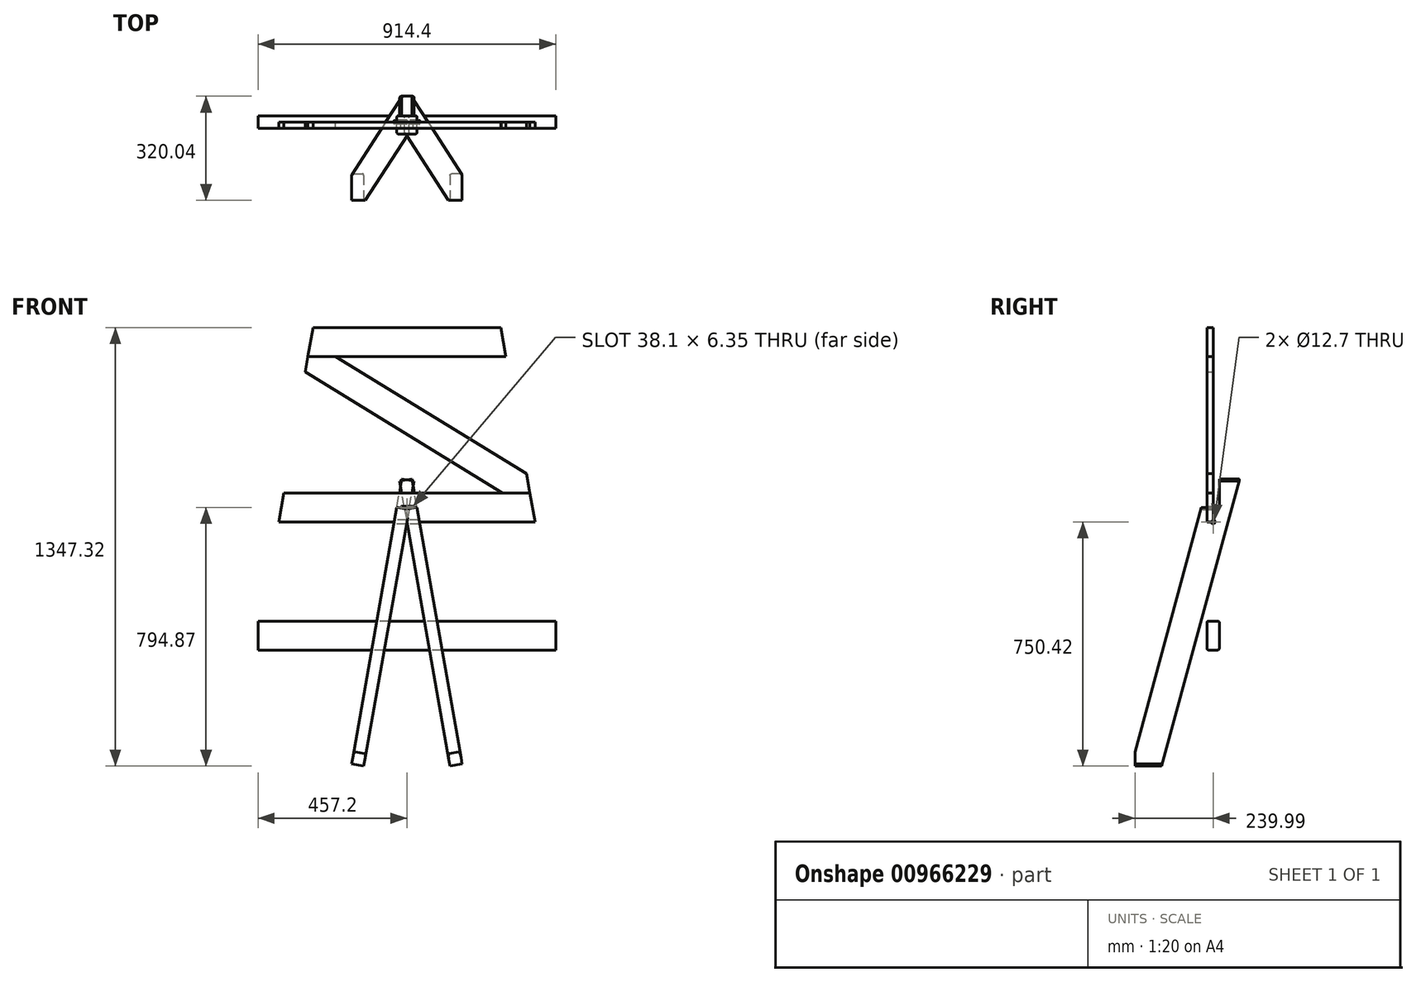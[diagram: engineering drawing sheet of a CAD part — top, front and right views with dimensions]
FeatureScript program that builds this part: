
annotation { "Feature Type Name" : "Feature", "Feature Type Description" : "" }
export const myFeature = defineFeature(function(context is Context, id is Id, definition is map)
    precondition{}
    {
        {
            var Q0;
            Q0=qCreatedBy(makeId("Front.planeOp"),FACE);
            var sketch = newSketch(context, id + "F0", { "sketchPlane" : qUnion([Q0])});
            skLineSegment(sketch, "E0", {"start": v(0, 0) * mm, "end": v(74.84, 13.2) * mm, "construction": true});
            skLineSegment(sketch, "E1", {"start": v(0, 0) * mm, "end": v(74.84, 0) * mm, "construction": true});
            skLineSegment(sketch, "E2", {"start": v(0, 0) * mm, "end": v(74.84, -13.2) * mm, "construction": true});
            skSolve(sketch);
        }
        {
            var Q0;
            Q0=sQuery(id+"F0.wireOp",EDGE,"E0");
            var Q1;
            Q1=sQuery(id+"F0.wireOp",VERTEX,"E0.start");
            cPlane(context, id + "F1", {"entities" : qUnion([Q0, Q1]), "cplaneType" : CPlaneType.LINE_POINT, "offset" : 25.4 * mm, "width" : 152.4 * mm, "height" : 152.4 * mm});
        }
        {
            var Q0;
            Q0=sQuery(id+"F0.wireOp",EDGE,"E2");
            var Q1;
            Q1=sQuery(id+"F0.wireOp",VERTEX,"E0.start");
            cPlane(context, id + "F2", {"entities" : qUnion([Q0, Q1]), "cplaneType" : CPlaneType.LINE_POINT, "offset" : 25.4 * mm, "width" : 152.4 * mm, "height" : 152.4 * mm});
        }
        {
            var Q0;
            Q0=qCreatedBy(id+"F1.planeOp",FACE);
            var sketch = newSketch(context, id + "F3", { "sketchPlane" : qUnion([Q0])});
            skLineSegment(sketch, "E3", {"start": v(10.2, 38.1) * mm, "end": v(-204.18, -762) * mm, "construction": true});
            skLineSegment(sketch, "E4", {"start": v(0, 0) * mm, "end": v(0, -762) * mm, "construction": true});
            skLineSegment(sketch, "E5.0", {"start": v(-35.8, 38.1) * mm, "end": v(-239.99, -723.9) * mm});
            skLineSegment(sketch, "E6.0", {"start": v(80.05, 127) * mm, "end": v(-158.16, -762) * mm});
            skLineSegment(sketch, "E7", {"start": v(-158.16, -762) * mm, "end": v(0, -762) * mm, "construction": true});
            skLineSegment(sketch, "E8", {"start": v(0, 0) * mm, "end": v(0, 239.53) * mm, "construction": true});
            skLineSegment(sketch, "E9.0", {"start": v(19.05, 38.1) * mm, "end": v(19.05, 127) * mm});
            skLineSegment(sketch, "E10", {"start": v(-35.8, 38.1) * mm, "end": v(19.05, 38.1) * mm});
            skLineSegment(sketch, "E11", {"start": v(19.05, 127) * mm, "end": v(80.05, 127) * mm});
            skLineSegment(sketch, "E12", {"start": v(-239.99, -723.9) * mm, "end": v(-239.99, -762) * mm});
            skPoint(sketch, "E13.orphan", {"position": v(-250.2, -762) * mm});
            skLineSegment(sketch, "E14", {"start": v(-158.16, -762) * mm, "end": v(-239.99, -762) * mm});
            skLineSegment(sketch, "E15", {"start": v(-149.99, 0) * mm, "end": v(149.99, 0) * mm, "construction": true});
            skSolve(sketch);
        }
        {
            var Q0;
            Q0=qCreatedBy(id+"F2.planeOp",FACE);
            var sketch = newSketch(context, id + "F4", { "sketchPlane" : qUnion([Q0])});
            skLineSegment(sketch, "E16", {"start": v(10.2, 38.1) * mm, "end": v(-204.18, -762) * mm, "construction": true});
            skLineSegment(sketch, "E17", {"start": v(0, 0) * mm, "end": v(0, -762) * mm, "construction": true});
            skLineSegment(sketch, "E18.0", {"start": v(-35.8, 38.1) * mm, "end": v(-239.99, -723.9) * mm});
            skLineSegment(sketch, "E19.0", {"start": v(80.05, 127) * mm, "end": v(-158.16, -762) * mm});
            skLineSegment(sketch, "E20", {"start": v(-158.16, -762) * mm, "end": v(0, -762) * mm, "construction": true});
            skLineSegment(sketch, "E21", {"start": v(0, 0) * mm, "end": v(0, 499.08) * mm, "construction": true});
            skLineSegment(sketch, "E22.0", {"start": v(19.05, 38.1) * mm, "end": v(19.05, 127) * mm});
            skLineSegment(sketch, "E23", {"start": v(-35.8, 38.1) * mm, "end": v(19.05, 38.1) * mm});
            skLineSegment(sketch, "E24", {"start": v(19.05, 127) * mm, "end": v(80.05, 127) * mm});
            skLineSegment(sketch, "E25", {"start": v(-239.99, -723.9) * mm, "end": v(-239.99, -762) * mm});
            skPoint(sketch, "E26.orphan", {"position": v(-250.2, -762) * mm});
            skLineSegment(sketch, "E27", {"start": v(-158.16, -762) * mm, "end": v(-239.99, -762) * mm});
            skLineSegment(sketch, "E28", {"start": v(-106.86, 0) * mm, "end": v(106.86, 0) * mm, "construction": true});
            skSolve(sketch);
        }
        {
            var Q0;
            Q0 = qSketchRegion(id + "F3", true);
            extrude(context, id + "F5", {"entities" : qUnion([Q0]), "depth" : 38.1 * mm, "offsetDistance" : 25.4 * mm});
        }
        {
            var Q0;
            Q0 = qSketchRegion(id + "F4", true);
            extrude(context, id + "F6", {"entities" : qUnion([Q0]), "oppositeDirection" : true, "depth" : 38.1 * mm, "offsetDistance" : 25.4 * mm});
        }
        {
            var Q0;
            Q0=makeQuery(id+"F5.opExtrude","SWEPT_EDGE",EDGE,{"disambiguationData":[OSD([sQuery(id+"F3.wireOp",EDGE,"E9.0"),sQuery(id+"F3.wireOp",EDGE,"E10")])]});
            var Q1;
            Q1=makeQuery(id+"F6.opExtrude","SWEPT_EDGE",EDGE,{"disambiguationData":[OSD([sQuery(id+"F4.wireOp",EDGE,"E22.0"),sQuery(id+"F4.wireOp",EDGE,"E23")])]});
            fillet(context, id + "F7", {"entities" : qUnion([Q0, Q1]), "tangentPropagation" : true, "radius" : 6.35 * mm, "defaultsChanged" : false, "vertexSettings" : [], "allowEdgeOverflow" : false});
        }
        {
            var Q0;
            Q0=qCreatedBy(makeId("Right.planeOp"),FACE);
            var sketch = newSketch(context, id + "F8", { "sketchPlane" : qUnion([Q0])});
            skCircle(sketch, "E29", {"center": v(0, 0) * mm, "radius": 6.35 * mm});
            skSolve(sketch);
        }
        {
            var Q0;
            Q0 = qSketchRegion(id + "F8", true);
            extrude(context, id + "F9", {"entities" : qUnion([Q0]), "operationType" : NewBodyOperationType.REMOVE, "endBound" : BoundingType.THROUGH_ALL, "depth" : 25.4 * mm, "offsetDistance" : 25.4 * mm, "hasSecondDirection" : true, "secondDirectionBound" : SecondDirectionBoundingType.THROUGH_ALL, "secondDirectionOppositeDirection" : true, "secondDirectionDepth" : 25.4 * mm});
        }
        {
            var Q0;
            Q0=qCreatedBy(makeId("Front.planeOp"),FACE);
            var sketch = newSketch(context, id + "F10", { "sketchPlane" : qUnion([Q0])});
            skLineSegment(sketch, "E30.0", {"start": v(-378.02, 88.9) * mm, "end": v(378.02, 88.9) * mm});
            skLineSegment(sketch, "E31.0", {"start": v(-393.7, 0) * mm, "end": v(393.7, 0) * mm});
            skLineSegment(sketch, "E32", {"start": v(-393.7, 0) * mm, "end": v(-378.02, 88.9) * mm});
            skLineSegment(sketch, "E33", {"start": v(378.02, 88.9) * mm, "end": v(393.7, 0) * mm});
            skLineSegment(sketch, "E34.bottom", {"start": v(15.87, 41.27) * mm, "end": v(-15.88, 41.27) * mm});
            skLineSegment(sketch, "E34.top", {"start": v(15.87, 47.62) * mm, "end": v(-15.88, 47.62) * mm});
            skLineSegment(sketch, "E34.left", {"start": v(19.05, 44.45) * mm, "end": v(19.05, 44.45) * mm});
            skLineSegment(sketch, "E34.right", {"start": v(-19.05, 44.45) * mm, "end": v(-19.05, 44.45) * mm});
            skPoint(sketch, "E34.middle", {"position": v(0, 44.45) * mm});
            skPoint(sketch, "E35.visualSharp", {"position": v(-19.05, 47.62) * mm});
            skArc(sketch, "E35.filletArc", {"start": v(-15.88, 47.62) * mm, "mid": v(-18.12, 46.7) * mm, "end": v(-19.05, 44.45) * mm});
            skPoint(sketch, "E36.visualSharp", {"position": v(-19.05, 41.27) * mm});
            skArc(sketch, "E36.filletArc", {"start": v(-19.05, 44.45) * mm, "mid": v(-18.12, 42.2) * mm, "end": v(-15.88, 41.27) * mm});
            skPoint(sketch, "E37.visualSharp", {"position": v(19.05, 41.27) * mm});
            skArc(sketch, "E37.filletArc", {"start": v(15.87, 41.27) * mm, "mid": v(18.12, 42.2) * mm, "end": v(19.05, 44.45) * mm});
            skPoint(sketch, "E38.visualSharp", {"position": v(19.05, 47.62) * mm});
            skArc(sketch, "E38.filletArc", {"start": v(19.05, 44.45) * mm, "mid": v(18.12, 46.7) * mm, "end": v(15.87, 47.62) * mm});
            skSolve(sketch);
        }
        {
            var Q0;
            Q0=makeQuery(id+"F10.imprint","IMPRINT",FACE,{"disambiguationData":[TD([[makeQuery(id+"F10.imprint","IMPRINT",EDGE,{"derivedFrom":sQuery(id+"F10.wireOp",EDGE,"E30.0")}),-1.0]])]});
            extrude(context, id + "F11", {"entities" : qUnion([Q0]), "depth" : 19.05 * mm, "offsetDistance" : 25.4 * mm});
        }
        {
            var Q0;
            Q0=qCreatedBy(makeId("Front.planeOp"),FACE);
            var sketch = newSketch(context, id + "F12", { "sketchPlane" : qUnion([Q0])});
            skLineSegment(sketch, "E39.0", {"start": v(-378.02, 88.9) * mm, "end": v(378.02, 88.9) * mm});
            skLineSegment(sketch, "E40", {"start": v(-378.02, 88.9) * mm, "end": v(-288.45, 596.9) * mm, "construction": true});
            skLineSegment(sketch, "E41", {"start": v(-288.45, 596.9) * mm, "end": v(288.45, 596.9) * mm});
            skLineSegment(sketch, "E42", {"start": v(288.45, 596.9) * mm, "end": v(378.02, 88.9) * mm, "construction": true});
            skLineSegment(sketch, "E43.0", {"start": v(-304.13, 508) * mm, "end": v(304.13, 508) * mm});
            skLineSegment(sketch, "E44", {"start": v(-288.45, 596.9) * mm, "end": v(-304.13, 508) * mm});
            skLineSegment(sketch, "E45", {"start": v(288.45, 596.9) * mm, "end": v(304.13, 508) * mm});
            skSolve(sketch);
        }
        {
            var Q0;
            Q0=makeQuery(id+"F12.imprint","IMPRINT",FACE,{"disambiguationData":[TD([[makeQuery(id+"F12.imprint","IMPRINT",EDGE,{"derivedFrom":sQuery(id+"F12.wireOp",EDGE,"E41")}),-1.0]])]});
            extrude(context, id + "F13", {"entities" : qUnion([Q0]), "depth" : 19.05 * mm, "offsetDistance" : 25.4 * mm});
        }
        {
            var Q0;
            Q0=qCreatedBy(makeId("Front.planeOp"),FACE);
            var sketch = newSketch(context, id + "F14", { "sketchPlane" : qUnion([Q0])});
            skLineSegment(sketch, "E46.0", {"start": v(-304.13, 508) * mm, "end": v(304.13, 508) * mm});
            skLineSegment(sketch, "E47.0", {"start": v(293.11, 88.9) * mm, "end": v(378.02, 88.9) * mm});
            skLineSegment(sketch, "E48", {"start": v(-304.13, 508) * mm, "end": v(378.02, 88.9) * mm, "construction": true});
            skLineSegment(sketch, "E49.0", {"start": v(-219.21, 508) * mm, "end": v(367.7, 147.4) * mm});
            skLineSegment(sketch, "E50.0", {"start": v(-312.43, 460.93) * mm, "end": v(293.11, 88.9) * mm});
            skLineSegment(sketch, "E51", {"start": v(-304.13, 508) * mm, "end": v(-312.43, 460.93) * mm});
            skLineSegment(sketch, "E52", {"start": v(378.02, 88.9) * mm, "end": v(367.7, 147.4) * mm});
            skLineSegment(sketch, "E53", {"start": v(-304.13, 508) * mm, "end": v(-219.21, 508) * mm});
            skLineSegment(sketch, "E54", {"start": v(378.02, 88.9) * mm, "end": v(293.11, 88.9) * mm});
            skPoint(sketch, "E55.orphan", {"position": v(-378.02, 88.9) * mm});
            skSolve(sketch);
        }
        {
            var Q0;
            Q0 = qSketchRegion(id + "F14", true);
            extrude(context, id + "F15", {"entities" : qUnion([Q0]), "depth" : 19.05 * mm, "offsetDistance" : 25.4 * mm});
        }
        {
            var Q0;
            Q0=qCreatedBy(makeId("Front.planeOp"),FACE);
            var sketch = newSketch(context, id + "F16", { "sketchPlane" : qUnion([Q0])});
            skLineSegment(sketch, "E56.bottom", {"start": v(457.2, -393.7) * mm, "end": v(-457.2, -393.7) * mm});
            skLineSegment(sketch, "E56.top", {"start": v(457.2, -304.8) * mm, "end": v(-457.2, -304.8) * mm});
            skLineSegment(sketch, "E56.left", {"start": v(457.2, -393.7) * mm, "end": v(457.2, -304.8) * mm});
            skLineSegment(sketch, "E56.right", {"start": v(-457.2, -393.7) * mm, "end": v(-457.2, -304.8) * mm});
            skPoint(sketch, "E56.middle", {"position": v(0, -349.25) * mm});
            skSolve(sketch);
        }
        {
            var Q0;
            Q0 = qSketchRegion(id + "F16", true);
            extrude(context, id + "F17", {"entities" : qUnion([Q0]), "endBound" : BoundingType.SYMMETRIC, "depth" : 38.1 * mm, "offsetDistance" : 25.4 * mm});
        }
        {
            var Q0;
            Q0=makeQuery(id+"F5.opExtrude","CAP_EDGE",EDGE,{"disambiguationData":[OSD([sQuery(id+"F3.wireOp",EDGE,"E5.0")])],"isStart":false});
            var Q1;
            Q1=makeQuery(id+"F5.opExtrude","CAP_EDGE",EDGE,{"disambiguationData":[OSD([sQuery(id+"F3.wireOp",EDGE,"E5.0")])],"isStart":true});
            var Q2;
            Q2=makeQuery(id+"F5.opExtrude","CAP_EDGE",EDGE,{"disambiguationData":[OSD([sQuery(id+"F3.wireOp",EDGE,"E6.0")])],"isStart":false});
            var Q3;
            Q3=makeQuery(id+"F5.opExtrude","CAP_EDGE",EDGE,{"disambiguationData":[OSD([sQuery(id+"F3.wireOp",EDGE,"E6.0")])],"isStart":true});
            var Q4;
            Q4=makeQuery(id+"F5.opExtrude","SWEPT_EDGE",EDGE,{"disambiguationData":[OSD([sQuery(id+"F3.wireOp",EDGE,"E9.0"),sQuery(id+"F3.wireOp",EDGE,"E10")])]});
            var Q5;
            Q5=makeQuery(id+"F6.opExtrude","CAP_EDGE",EDGE,{"disambiguationData":[OSD([sQuery(id+"F4.wireOp",EDGE,"E18.0")])],"isStart":true});
            var Q6;
            Q6=makeQuery(id+"F6.opExtrude","CAP_EDGE",EDGE,{"disambiguationData":[OSD([sQuery(id+"F4.wireOp",EDGE,"E19.0")])],"isStart":true});
            var Q7;
            Q7=makeQuery(id+"F6.opExtrude","CAP_EDGE",EDGE,{"disambiguationData":[OSD([sQuery(id+"F4.wireOp",EDGE,"E18.0")])],"isStart":false});
            var Q8;
            Q8=makeQuery(id+"F6.opExtrude","CAP_EDGE",EDGE,{"disambiguationData":[OSD([sQuery(id+"F4.wireOp",EDGE,"E19.0")])],"isStart":false});
            var Q9;
            Q9=makeQuery(id+"F17.opExtrude","CAP_EDGE",EDGE,{"disambiguationData":[OSD([sQuery(id+"F16.wireOp",EDGE,"E56.bottom")])],"isStart":false});
            var Q10;
            Q10=makeQuery(id+"F17.opExtrude","CAP_EDGE",EDGE,{"disambiguationData":[OSD([sQuery(id+"F16.wireOp",EDGE,"E56.top")])],"isStart":false});
            var Q11;
            Q11=makeQuery(id+"F17.opExtrude","CAP_EDGE",EDGE,{"disambiguationData":[OSD([sQuery(id+"F16.wireOp",EDGE,"E56.bottom")])],"isStart":true});
            var Q12;
            Q12=makeQuery(id+"F17.opExtrude","CAP_EDGE",EDGE,{"disambiguationData":[OSD([sQuery(id+"F16.wireOp",EDGE,"E56.top")])],"isStart":true});
            fillet(context, id + "F18", {"entities" : qUnion([Q0, Q1, Q2, Q3, Q4, Q5, Q6, Q7, Q8, Q9, Q10, Q11, Q12]), "radius" : 4.78 * mm, "tangentPropagation" : true, "allowEdgeOverflow" : false});
        }
    });
